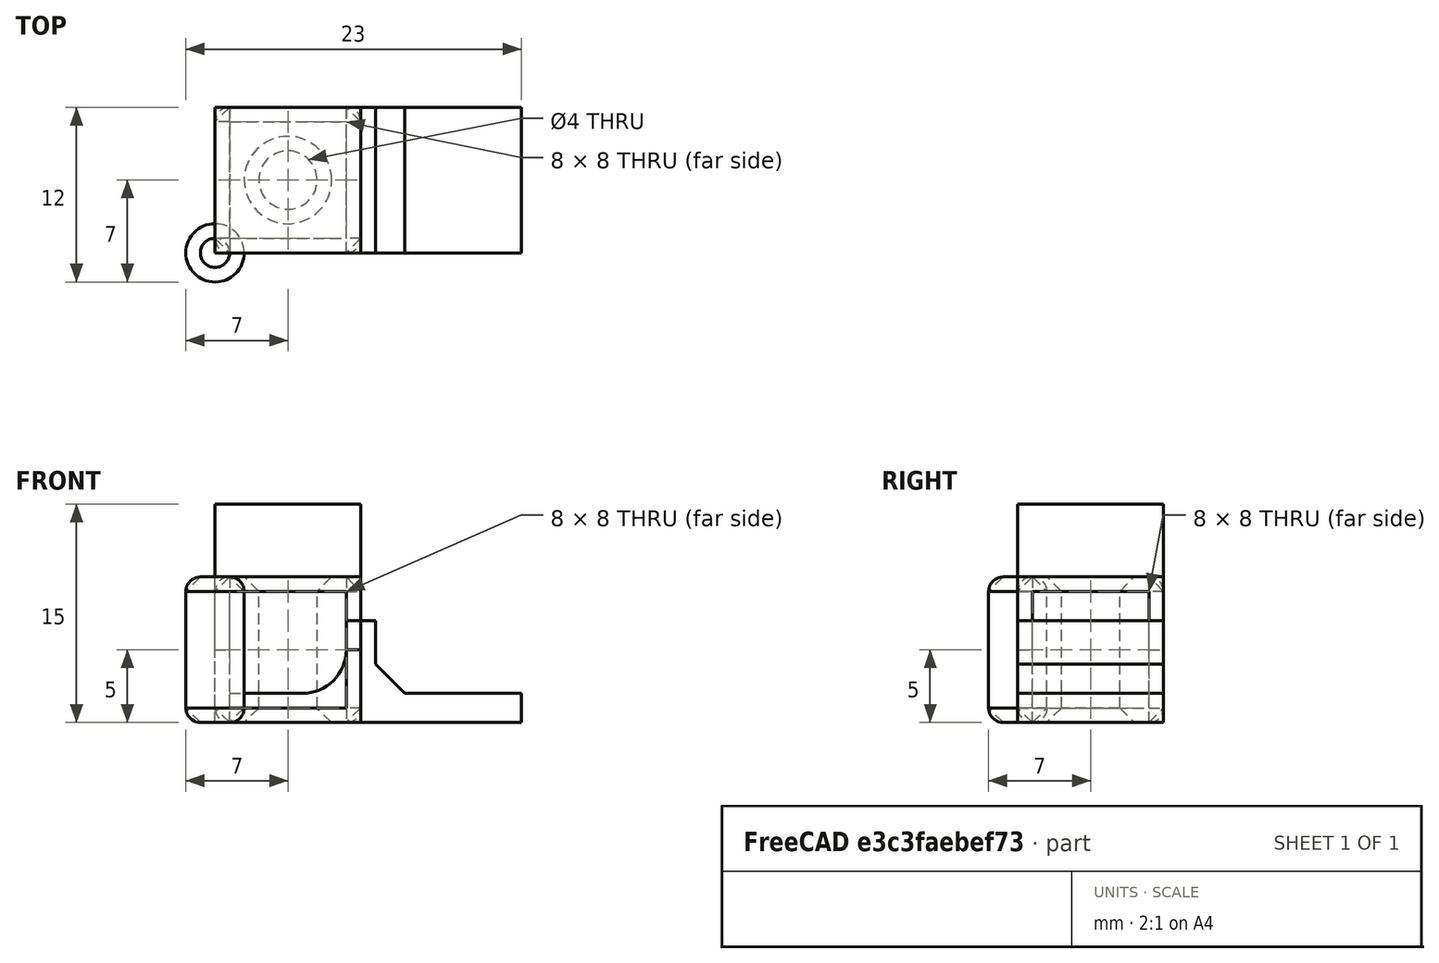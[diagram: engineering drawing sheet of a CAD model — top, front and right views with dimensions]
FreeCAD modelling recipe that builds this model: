
FCSTD DOCUMENT  (FreeCAD 0.18R16146 (Git))
Label: refuerzos,chaflanes,redondeos_dani
License: All rights reserved
LicenseURL: http://en.wikipedia.org/wiki/All_rights_reserved
objects: Part::Box×8, Part::Cut×4, Part::Chamfer×4, Part::Fillet×3, Part::Cylinder×3, Part::MultiFuse×1
note: 23 computed .brp shape members not serialized (recipe doc carries the construction recipe); baked Part::Feature solids carry a one-line shape summary decoded from their .brp

FEATURE [Part::Box] Box  label="Cubo"
  AttacherType = Attacher::AttachEngine3D
  Height = 10
  Length = 10
  Width = 10
FEATURE [Part::Fillet] Fillet
  Base = -> Box
  Edges = 12 edges r=1: [Edge1,Edge2,Edge3,Edge4,Edge5,Edge6,Edge7,Edge8,Edge9,Edge10,Edge11,Edge12]
FEATURE [Part::Box] Box001  label="Cubo"
  AttacherType = Attacher::AttachEngine3D
  Height = 10
  Length = 10
  Width = 10
FEATURE [Part::Cut] Cut
  Base = -> Box001
  Refine = true
  Tool = -> Fillet
FEATURE [Part::Box] Box002  label="Cubo"
  AttacherType = Attacher::AttachEngine3D
  Height = 10
  Length = 10
  Width = 10
FEATURE [Part::Chamfer] Chamfer
  Base = -> Box002
  Edges = 12 edges r=1: [Edge1,Edge2,Edge3,Edge4,Edge5,Edge6,Edge7,Edge8,Edge9,Edge10,Edge11,Edge12]
FEATURE [Part::Box] Box003  label="Cubo"
  AttacherType = Attacher::AttachEngine3D
  Height = 10
  Length = 10
  Placement = pos=(0,0,5) rot=(0,0,1;0rad)
  Width = 10
FEATURE [Part::Cut] Cut001
  Base = -> Box003
  Refine = true
  Tool = -> Chamfer
FEATURE [Part::Box] Box004  label="Cubo"
  AttacherType = Attacher::AttachEngine3D
  Height = 10
  Length = 10
  Width = 10
FEATURE [Part::Cylinder] Cylinder  label="Cilindro"
  Angle = 360
  AttacherType = Attacher::AttachEngine3D
  Height = 10
  Placement = pos=(5,5,0) rot=(0,0,1;0rad)
  Radius = 2
FEATURE [Part::Cut] Cut002
  Base = -> Box004
  Refine = true
  Tool = -> Cylinder
FEATURE [Part::Chamfer] Chamfer001
  Base = -> Cut002
  Edges = 14 edges r=1: [Edge1,Edge2,Edge3,Edge4,Edge5,Edge6,Edge7,Edge8,Edge9,Edge10,Edge11,Edge12,Edge13,Edge14]
FEATURE [Part::Cylinder] Cylinder001  label="Cilindro"
  Angle = 360
  AttacherType = Attacher::AttachEngine3D
  Height = 10
  Radius = 2
FEATURE [Part::Fillet] Fillet001
  Base = -> Cylinder001
  Edges = 2 edges r=1: [Edge1,Edge3]
FEATURE [Part::Cylinder] Cylinder002  label="Cilindro"
  Angle = 360
  AttacherType = Attacher::AttachEngine3D
  Height = 10
  Radius = 2
FEATURE [Part::Chamfer] Chamfer002
  Base = -> Cylinder002
  Edges = 2 edges r=1: [Edge1,Edge3]
FEATURE [Part::Box] Box005  label="Cubo"
  AttacherType = Attacher::AttachEngine3D
  Height = 7
  Length = 20
  Placement = pos=(1,0,0) rot=(0,0,1;0rad)
  Width = 10
FEATURE [Part::Box] Box006  label="Cubo"
  AttacherType = Attacher::AttachEngine3D
  Height = 5
  Length = 10
  Placement = pos=(-1,0,2) rot=(0,0,1;0rad)
  Width = 10
FEATURE [Part::Box] Box007  label="Cubo"
  AttacherType = Attacher::AttachEngine3D
  Height = 5
  Length = 10
  Placement = pos=(11,0,2) rot=(0,0,1;0rad)
  Width = 10
FEATURE [Part::MultiFuse] Fusion
  Refine = true
  Shapes = -> [Box006,Box007]
FEATURE [Part::Cut] Cut003
  Base = -> Box005
  Refine = true
  Tool = -> Fusion
FEATURE [Part::Chamfer] Chamfer003
  Base = -> Cut003
  Edges = 1 edges r=2: [Edge22]
FEATURE [Part::Fillet] Fillet002
  Base = -> Chamfer003
  Edges = 1 edges r=3: [Edge26]
